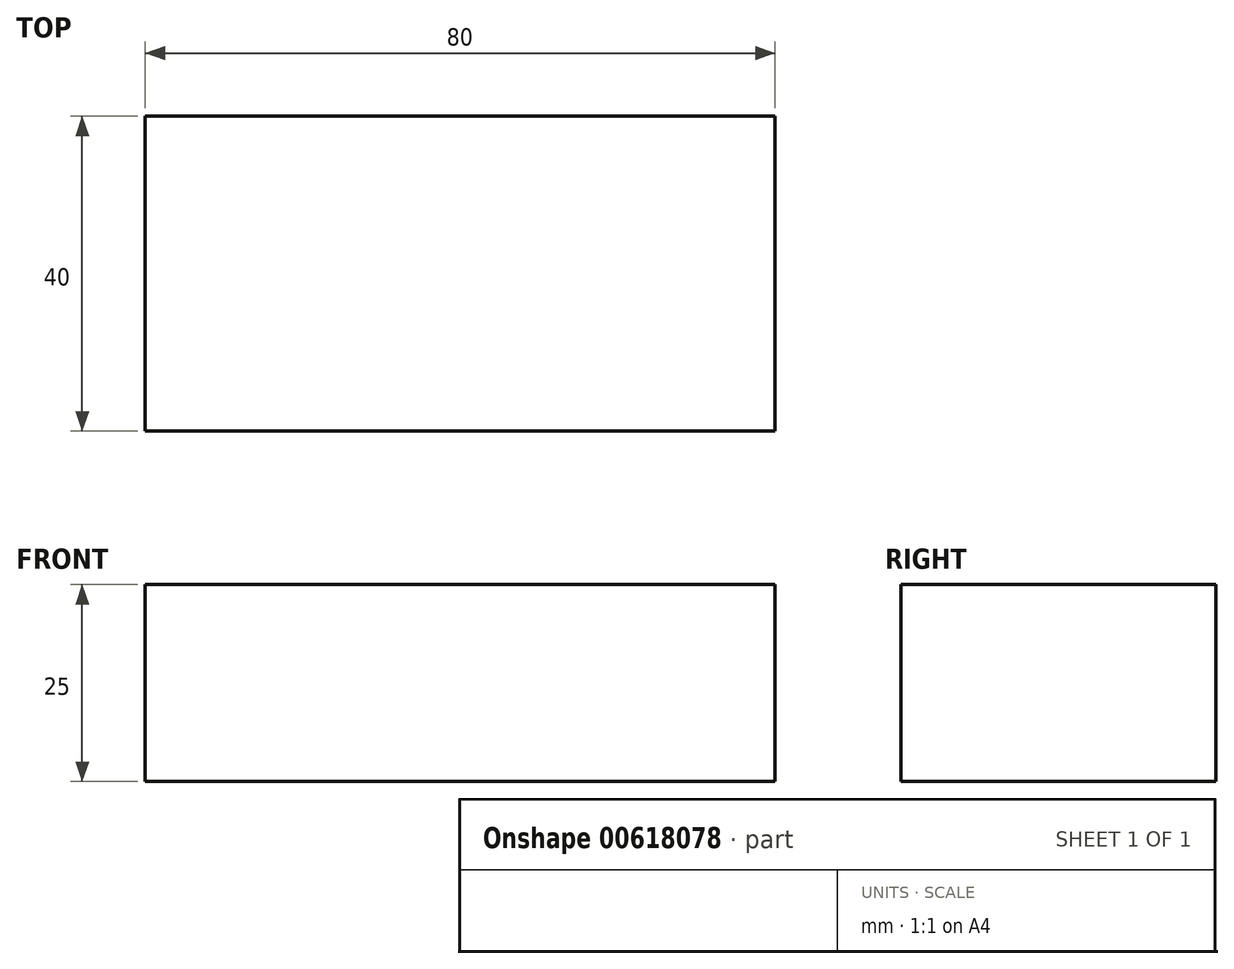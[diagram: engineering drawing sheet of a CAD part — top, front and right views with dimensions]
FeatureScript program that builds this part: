
annotation { "Feature Type Name" : "Feature", "Feature Type Description" : "" }
export const myFeature = defineFeature(function(context is Context, id is Id, definition is map)
    precondition{}
    {
        {
            var Q0;
            Q0=qCreatedBy(makeId("Top.planeOp"),FACE);
            var sketch = newSketch(context, id + "F0", { "sketchPlane" : qUnion([Q0])});
            skLineSegment(sketch, "E0.bottom", {"start": v(0, 0) * mm, "end": v(80, 0) * mm});
            skLineSegment(sketch, "E0.top", {"start": v(0, 40) * mm, "end": v(80, 40) * mm});
            skLineSegment(sketch, "E0.left", {"start": v(0, 0) * mm, "end": v(0, 40) * mm});
            skLineSegment(sketch, "E0.right", {"start": v(80, 0) * mm, "end": v(80, 40) * mm});
            skSolve(sketch);
        }
        {
            var Q0;
            Q0=makeQuery(id+"F0.imprint","IMPRINT",FACE,{"disambiguationData":[TD([[makeQuery(id+"F0.imprint","IMPRINT",EDGE,{"derivedFrom":sQuery(id+"F0.wireOp",EDGE,"E0.bottom")}),1.0]])]});
            extrude(context, id + "F1", {"entities" : qUnion([Q0]), "depth" : 25 * mm, "offsetDistance" : 25 * mm});
        }
    });
